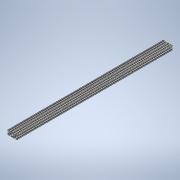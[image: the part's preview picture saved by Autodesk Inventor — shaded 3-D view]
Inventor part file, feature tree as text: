
AUTODESK INVENTOR PART (.ipt)
format: ipt  version: 2020 (Build 240168000, 168)  size: 339,456 bytes
history: native  units: in
note: dims shown in document units (in); Inventor stores cm internally (conversion verified against a paired STEP export)
features: sketch x2, extrude x1
ambient origin geometry x8: Origin, YZ Plane, XZ Plane, XY Plane, X Axis, Y Axis, Z Axis, Center Point
bodies: Solid1 (feature_tree)
feature tree (3):
  extrude  "Extrusion1"  [1 undecoded]
  sketch  "Sketch2"
  sketch  "Sketch1"  dims[d0=33.0in d1=0.0in]
note: 1 required parameter value undecoded (feature->parameter linkage not recoverable at this tier; creation-order binding heuristic only, values carry confidence <= 0.55)
